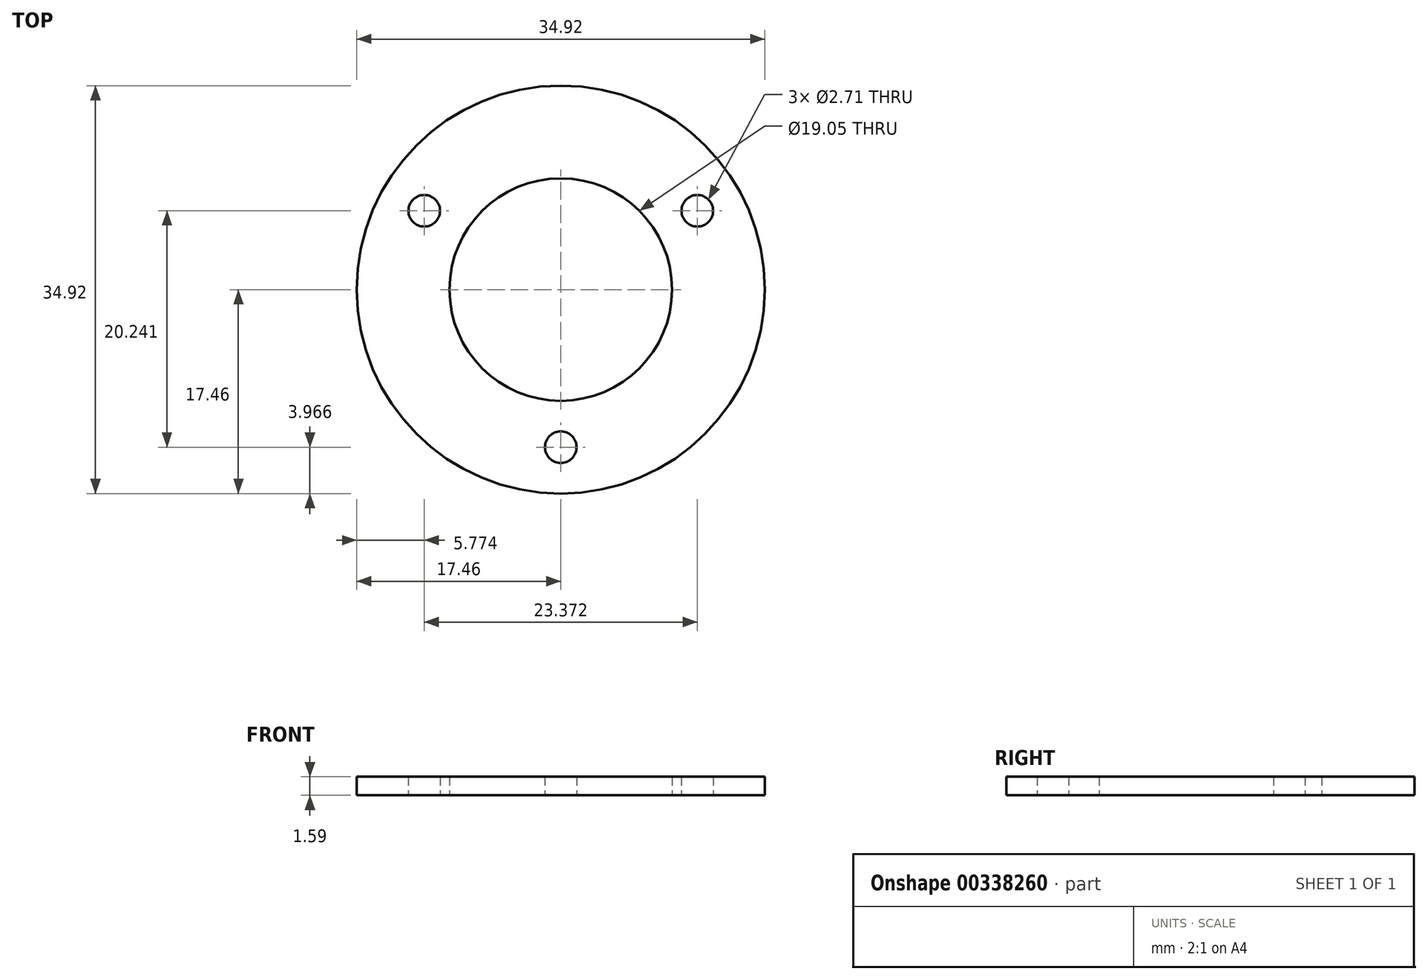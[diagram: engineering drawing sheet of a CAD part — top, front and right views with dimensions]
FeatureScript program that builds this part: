
annotation { "Feature Type Name" : "Feature", "Feature Type Description" : "" }
export const myFeature = defineFeature(function(context is Context, id is Id, definition is map)
    precondition{}
    {
        {
            var Q0;
            Q0=qCreatedBy(makeId("Top.planeOp"),FACE);
            var sketch = newSketch(context, id + "F0", { "sketchPlane" : qUnion([Q0])});
            skCircle(sketch, "E0", {"center": v(0, 0) * mm, "radius": 9.52 * mm});
            skCircle(sketch, "E1", {"center": v(0, 0) * mm, "radius": 17.46 * mm});
            skLineSegment(sketch, "E2", {"start": v(0, 0) * mm, "end": v(0, -13.5) * mm, "construction": true});
            skLineSegment(sketch, "E3", {"start": v(0, -13.5) * mm, "end": v(11.69, 6.75) * mm, "construction": true});
            skLineSegment(sketch, "E4", {"start": v(11.69, 6.75) * mm, "end": v(0, 0) * mm, "construction": true});
            skLineSegment(sketch, "E5", {"start": v(0, 0) * mm, "end": v(-11.69, 6.75) * mm, "construction": true});
            skLineSegment(sketch, "E6", {"start": v(-11.69, 6.75) * mm, "end": v(0, -13.5) * mm, "construction": true});
            skLineSegment(sketch, "E7", {"start": v(-11.69, 6.75) * mm, "end": v(11.69, 6.75) * mm, "construction": true});
            skCircle(sketch, "E8", {"center": v(0, -13.5) * mm, "radius": 3.97 * mm, "construction": true});
            skCircle(sketch, "E9", {"center": v(-11.69, 6.75) * mm, "radius": 1.35 * mm});
            skCircle(sketch, "E10", {"center": v(11.69, 6.75) * mm, "radius": 1.35 * mm});
            skCircle(sketch, "E11", {"center": v(0, -13.5) * mm, "radius": 1.35 * mm});
            skSolve(sketch);
        }
        {
            var Q0;
            Q0=qSketchRegion(id+"F0",true);
            extrude(context, id + "F1", {"entities" : qUnion([Q0]), "depth" : 1.59 * mm});
        }
    });
